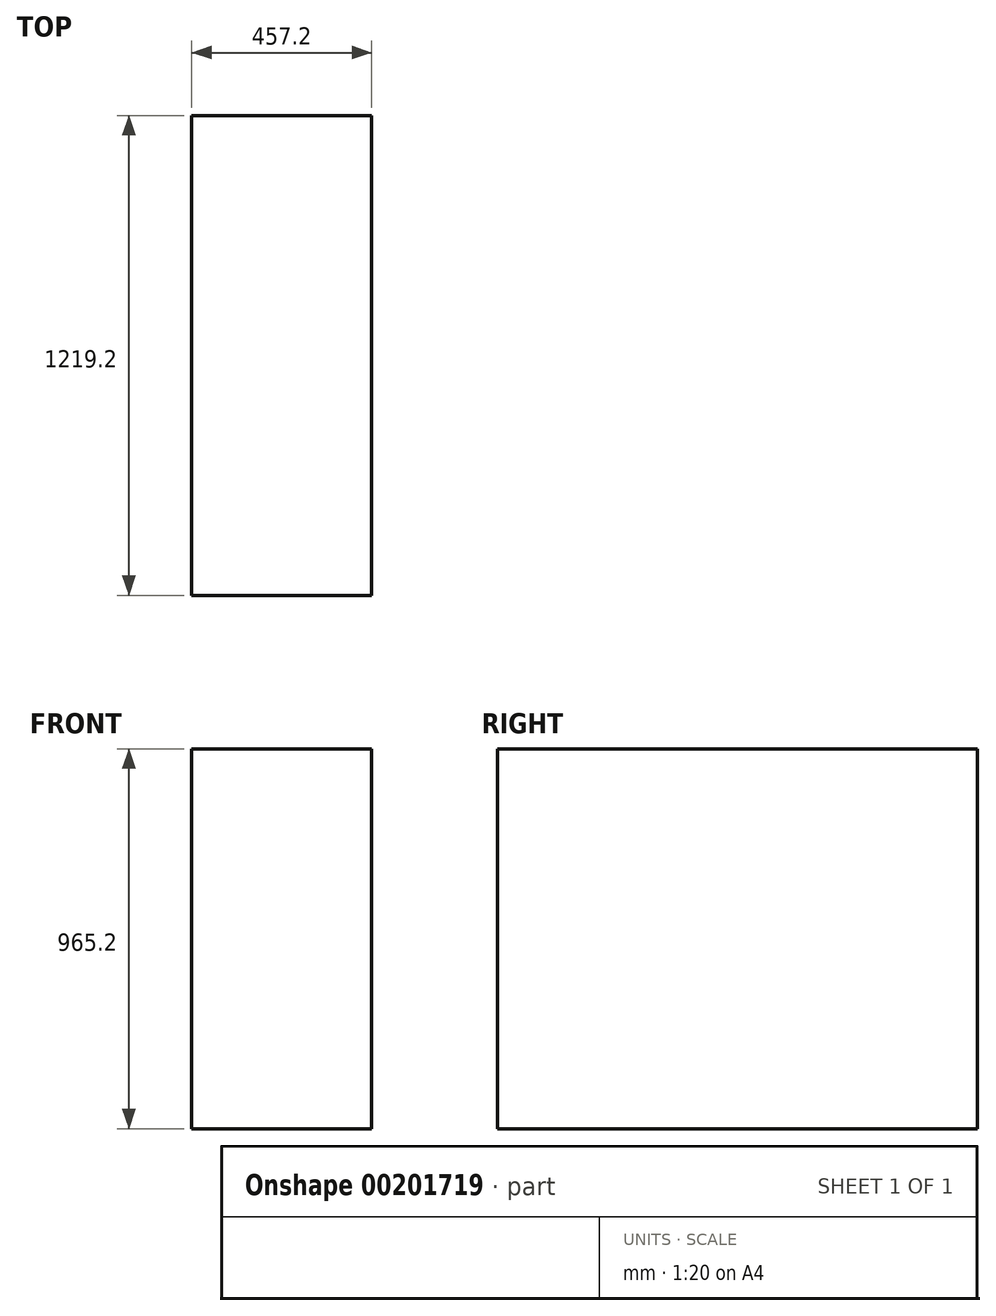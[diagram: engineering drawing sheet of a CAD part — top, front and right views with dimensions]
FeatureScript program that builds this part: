
annotation { "Feature Type Name" : "Feature", "Feature Type Description" : "" }
export const myFeature = defineFeature(function(context is Context, id is Id, definition is map)
    precondition{}
    {
        {
            var Q0;
            Q0=qCreatedBy(makeId("Top.planeOp"),FACE);
            var sketch = newSketch(context, id + "F0", { "sketchPlane" : qUnion([Q0])});
            skLineSegment(sketch, "E0.bottom", {"start": v(-228.6, 609.6) * mm, "end": v(228.6, 609.6) * mm});
            skLineSegment(sketch, "E0.top", {"start": v(-228.6, -609.6) * mm, "end": v(228.6, -609.6) * mm});
            skLineSegment(sketch, "E0.left", {"start": v(-228.6, 609.6) * mm, "end": v(-228.6, -609.6) * mm});
            skLineSegment(sketch, "E0.right", {"start": v(228.6, 609.6) * mm, "end": v(228.6, -609.6) * mm});
            skPoint(sketch, "E0.middle", {"position": v(0, 0) * mm});
            skSolve(sketch);
        }
        {
            var Q0;
            Q0=qSketchRegion(id+"F0",true);
            extrude(context, id + "F1", {"entities" : qUnion([Q0]), "depth" : 965.2 * mm});
        }
    });
